# Revit family: GEL_Ver.2.5
name_source: partatom
category: Windows
revit_build: Autodesk Revit Architecture 2014 (Build: 20130308_1515(x64)
units: mm (PartAtom-declared; Revit-internal decimal feet)

## types (1)
- GEL and VEA-VEB-VEC (MK08/MK35)
    2d details = http://www.velux.co.uk
    AcousticRating = 35
    Air permeability Class = 3
    Allowed Roof Slope = 35°-53°
    Angled bottom panel = 45.00°
    Apron Material = Aluminium. Color NCS 7500-N
    Bottom Void = 1429.192 mm
    Bottom Window Height = 1093.2 mm
    Bottom panel open = No
    Colour = Aluminium. Color NCS 7500-N
    Description = http://www.velux.co.uk
    Disclaimer = When installing VELUX roof windows the costumer must make sure to meet local applicable building and fire requirements. VELUX shall not be liable for the objects/drawings and the constructional quality of the installation. Please contact VELUX for technical specifications of VELUX roof windows, flashings, installations products and internal/external accessories.
    Documentation = http://www.professional.velux.co.uk
    Emergency exit = ??
    Features = Top/side hung roof terrase
    Finish = White paint color NCS 0500-N
    FireRating = E
    Fixed = No
    Function = Top and side hung roof terrase
    Glazing = Extra heat insulation (--65G)
    Handle left = No
    Handle right = Yes
    Height = 1355 mm  [stored 4.44554 ft]
    Installation instructions = http://www.velux.co.uk
    IsExternal = Yes
    Light transmittance = 0.69
    Manufacturer = VELUX A/S
    Manufacturer URL = www.VELUX.com
    Material = Aluminium. Color NCS 7500-N
    Material External = Aluminium. Color NCS 7500-N
    Material Internal = White paint color NCS 0500-N
    ModelReference = GEL and VEA, VEB, VEC size 780x1355/1088 (MK08/MK35)
    NominalHeight = 1355
    NominalWidth = 780
    Opening Lines = Yes
    Operation = Manuel
    Operation Mode = Manuel
    PerimeterGlazing m = 5.366
    PerimeterWindow m = 6.446
    Product certification = www.velux.com/ce
    Roof Slope Angle = 45.00°
    Rough Height = 1395 mm
    Rough Width = 820 mm  [stored 2.69029 ft]
    Shape = Rectangular
    Size = GEL and VEA, VEB, VEC size 780x1355/1088 (MK08/MK35)
    SmokeStop = No
    Sound Insulation db = 35
    Square Reveal Length = 150 mm
    Technical description = http://www.professional.velux.co.uk
    Thermal Resistance (R) = 0.8333333333
    ThermalBridge(Installation) W/mK = 0.09
    ThermalBridge(glazing) W/mK = 0.06
    ThermalTransmittance = 1.2
    Top panel open = No
    URL = www.VELUX.dk
    Ultraviolet Transmittance = 0.05
    Ventilations flap areal mm2 = 4600
    Warranty Years = 5 (10 with BDX)
    Water Tightness Class = 9A
    Width = 780 mm  [stored 2.55906 ft]
    Within Standard Sizes = Yes
    g-value = 0.5

note: [stored X ft] marks values corroborated as IEEE doubles in the binary element streams (Revit-internal decimal feet)

## geometry (parser evidence)
native form markers: Blend x10, Sweep x8
no freeform markers — native parametric forms only
